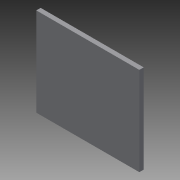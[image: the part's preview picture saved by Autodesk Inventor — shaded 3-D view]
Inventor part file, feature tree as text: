
AUTODESK INVENTOR PART (.ipt)
format: ipt  version: 2013 (Build 170138000, 138)  size: 66,048 bytes
history: native  units: in
note: dims shown in document units (in); Inventor stores cm internally (conversion verified against a paired STEP export)
features: extrude x1, sketch x1
ambient origin geometry x8: Origin, YZ Plane, XZ Plane, XY Plane, X Axis, Y Axis, Z Axis, Center Point
bodies: Solid1 (feature_tree)
feature tree (2):
  extrude  "Extrusion1"  Depth=0.25in TaperAngle=0.0deg
  sketch  "Sketch1"  dims[d0=5.8661in d1=0.25in d2=0.0in d3=5.0394in]
